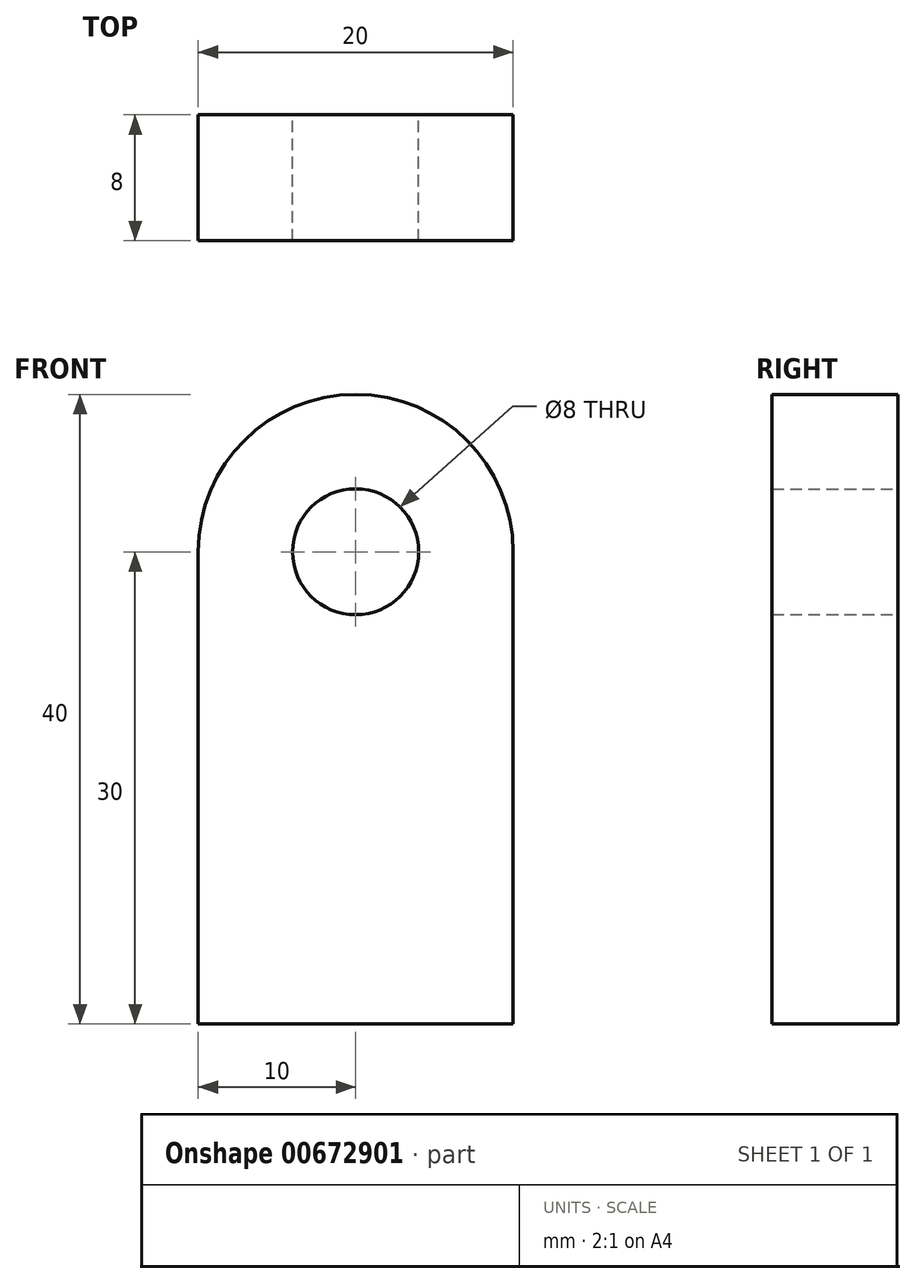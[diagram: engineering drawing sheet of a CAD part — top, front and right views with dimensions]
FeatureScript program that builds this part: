
annotation { "Feature Type Name" : "Feature", "Feature Type Description" : "" }
export const myFeature = defineFeature(function(context is Context, id is Id, definition is map)
    precondition{}
    {
        {
            var Q0;
            Q0=qCreatedBy(makeId("Front.planeOp"),FACE);
            var sketch = newSketch(context, id + "F0", { "sketchPlane" : qUnion([Q0])});
            skCircle(sketch, "E0", {"center": v(0, 30) * mm, "radius": 4 * mm});
            skArc(sketch, "E1", {"start": v(10, 30) * mm, "mid": v(0, 40) * mm, "end": v(-10, 30) * mm});
            skLineSegment(sketch, "E2", {"start": v(-10, 30) * mm, "end": v(-10, 0) * mm});
            skLineSegment(sketch, "E3", {"start": v(10, 30) * mm, "end": v(10, 0) * mm});
            skLineSegment(sketch, "E4", {"start": v(-10, 0) * mm, "end": v(10, 0) * mm});
            skSolve(sketch);
        }
        {
            var Q0;
            Q0 = qSketchRegion(id + "F0", true);
            extrude(context, id + "F1", {"entities" : qUnion([Q0]), "depth" : 8 * mm, "offsetDistance" : 25 * mm});
        }
    });
